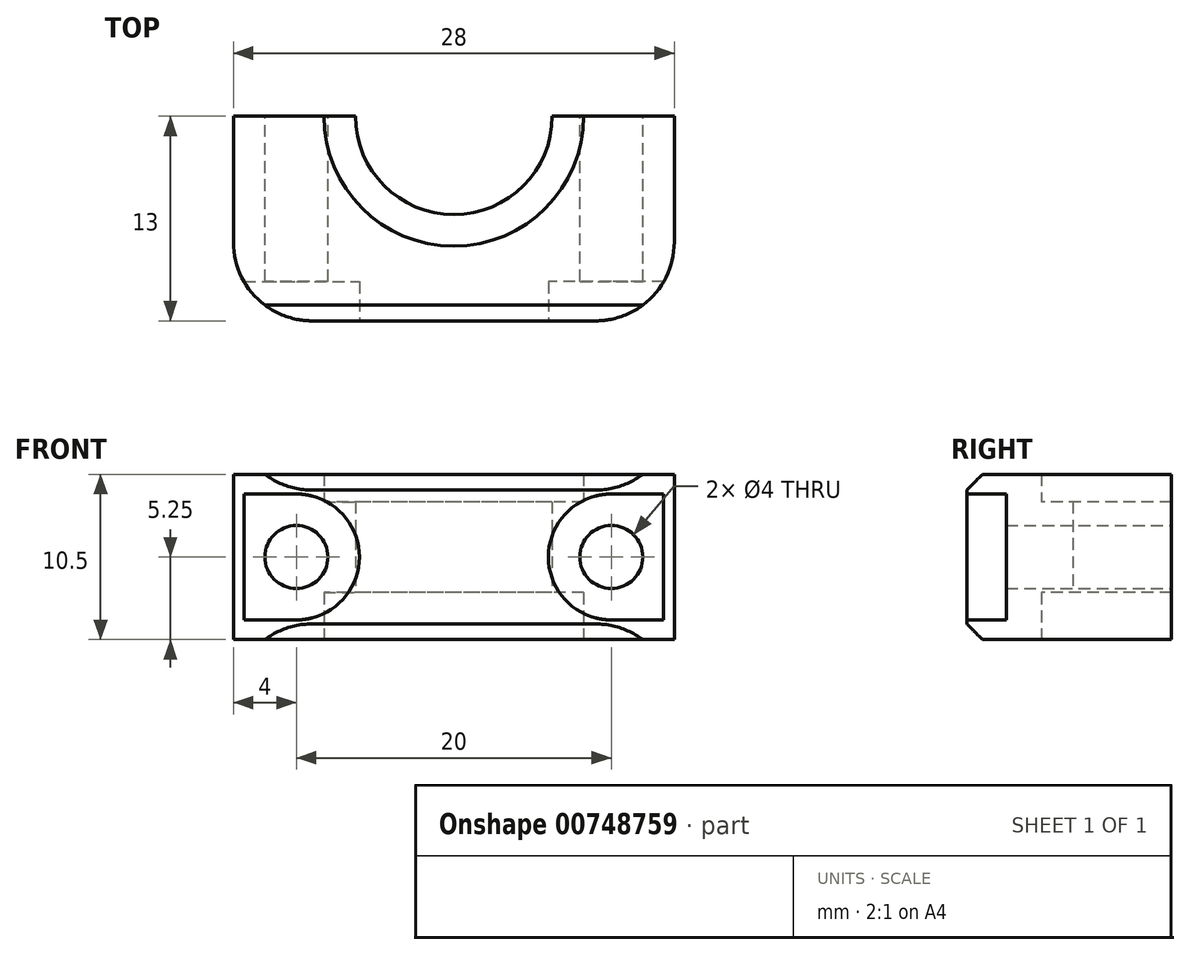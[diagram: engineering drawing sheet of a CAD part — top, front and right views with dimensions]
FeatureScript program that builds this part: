
annotation { "Feature Type Name" : "Feature", "Feature Type Description" : "" }
export const myFeature = defineFeature(function(context is Context, id is Id, definition is map)
    precondition{}
    {
        {
            var Q0;
            Q0=qCreatedBy(makeId("Front.planeOp"),FACE);
            var sketch = newSketch(context, id + "F0", { "sketchPlane" : qUnion([Q0])});
            skLineSegment(sketch, "E0", {"start": v(0, 5.25) * mm, "end": v(0, -5.25) * mm});
            skLineSegment(sketch, "E1", {"start": v(0, 5.25) * mm, "end": v(-14, 5.25) * mm});
            skLineSegment(sketch, "E2", {"start": v(-14, 5.25) * mm, "end": v(-14, -5.25) * mm});
            skLineSegment(sketch, "E3", {"start": v(0, -5.25) * mm, "end": v(-14, -5.25) * mm});
            skLineSegment(sketch, "E4", {"start": v(0, 3.5) * mm, "end": v(-8.25, 3.5) * mm});
            skLineSegment(sketch, "E5", {"start": v(-8.25, 3.5) * mm, "end": v(-8.25, 5.25) * mm});
            skLineSegment(sketch, "E6", {"start": v(0, -2.25) * mm, "end": v(-8.25, -2.25) * mm});
            skLineSegment(sketch, "E7", {"start": v(-8.25, -2.25) * mm, "end": v(-8.25, -5.25) * mm});
            skLineSegment(sketch, "E8", {"start": v(-6.25, -2.25) * mm, "end": v(-6.25, 3.5) * mm});
            skCircle(sketch, "E9", {"center": v(-10, 0) * mm, "radius": 2 * mm});
            skSolve(sketch);
        }
        {
            var Q0;
            {var subQ1=sQuery(id+"F0.wireOp",EDGE,"E2");Q0=makeQuery(id+"F0.imprint","IMPRINT",FACE,{"disambiguationData":[TD([[makeQuery(id+"F0.imprint","IMPRINT",EDGE,{"derivedFrom":subQ1}),1.0]])]});}
            var Q1;
            Q1=makeQuery(id+"F0.imprint","IMPRINT",FACE,{"disambiguationData":[TD([[makeQuery(id+"F0.imprint","IMPRINT",EDGE,{"derivedFrom":sQuery(id+"F0.wireOp",EDGE,"E9")}),1.0]])]});
            var Q2;
            {var subQ0=sQuery(id+"F0.wireOp",EDGE,"E5");Q2=makeQuery(id+"F0.imprint","IMPRINT",FACE,{"disambiguationData":[TD([[makeQuery(id+"F0.imprint","IMPRINT",EDGE,{"derivedFrom":subQ0}),-1.0]])]});}
            var Q3;
            {var subQ5=sQuery(id+"F0.wireOp",EDGE,"E8");Q3=makeQuery(id+"F0.imprint","IMPRINT",FACE,{"disambiguationData":[TD([[makeQuery(id+"F0.imprint","IMPRINT",EDGE,{"derivedFrom":subQ5}),-1.0]])]});}
            var Q4;
            {var subQ6=sQuery(id+"F0.wireOp",EDGE,"E7");Q4=makeQuery(id+"F0.imprint","IMPRINT",FACE,{"disambiguationData":[TD([[makeQuery(id+"F0.imprint","IMPRINT",EDGE,{"derivedFrom":subQ6}),1.0]])]});}
            extrude(context, id + "F1", {"entities" : qUnion([Q0, Q1, Q2, Q3, Q4]), "depth" : (8 + 5) * mm, "offsetDistance" : 25 * mm});
        }
        {
            var Q0;
            {var subQ0=sQuery(id+"F0.wireOp",EDGE,"E5");Q0=makeQuery(id+"F0.imprint","IMPRINT",FACE,{"disambiguationData":[TD([[makeQuery(id+"F0.imprint","IMPRINT",EDGE,{"derivedFrom":subQ0}),-1.0]])]});}
            var Q1;
            {var subQ5=sQuery(id+"F0.wireOp",EDGE,"E8");Q1=makeQuery(id+"F0.imprint","IMPRINT",FACE,{"disambiguationData":[TD([[makeQuery(id+"F0.imprint","IMPRINT",EDGE,{"derivedFrom":subQ5}),-1.0]])]});}
            var Q2;
            {var subQ6=sQuery(id+"F0.wireOp",EDGE,"E7");Q2=makeQuery(id+"F0.imprint","IMPRINT",FACE,{"disambiguationData":[TD([[makeQuery(id+"F0.imprint","IMPRINT",EDGE,{"derivedFrom":subQ6}),1.0]])]});}
            var Q3;
            Q3=sQuery(id+"F0.wireOp",EDGE,"E0");
            revolve(context, id + "F2", {"operationType" : NewBodyOperationType.REMOVE, "surfaceOperationType" : NewSurfaceOperationType.NEW, "entities" : qUnion([Q0, Q1, Q2]), "axis" : qUnion([Q3]), "revolveType" : RevolveType.FULL, "oppositeDirection" : true});
        }
        {
            var Q0;
            Q0=makeQuery(id+"F0.imprint","IMPRINT",FACE,{"disambiguationData":[TD([[makeQuery(id+"F0.imprint","IMPRINT",EDGE,{"derivedFrom":sQuery(id+"F0.wireOp",EDGE,"E9")}),1.0]])]});
            extrude(context, id + "F3", {"entities" : qUnion([Q0]), "operationType" : NewBodyOperationType.REMOVE, "depth" : 25 * mm, "offsetDistance" : 25 * mm});
        }
        {
            var Q0;
            Q0=makeQuery(id+"F1.opExtrude","CAP_EDGE",EDGE,{"disambiguationData":[OSD([sQuery(id+"F0.wireOp",EDGE,"E2")])],"isStart":false});
            fillet(context, id + "F4", {"entities" : qUnion([Q0]), "radius" : 5 * mm, "tangentPropagation" : true, "allowEdgeOverflow" : false});
        }
        {
            var Q0;
            {var subQ0=makeQuery(id+"F1.opExtrude","CAP_FACE",FACE,{"disambiguationData":[OSD([sQuery(id+"F0.wireOp",EDGE,"E0"),sQuery(id+"F0.wireOp",EDGE,"E1"),sQuery(id+"F0.wireOp",EDGE,"E2"),sQuery(id+"F0.wireOp",EDGE,"E3")])],"isStart":false});Q0=makeQuery(id+"F8.boolean.opBoolean","MERGE",FACE,{"derivedFrom":[subQ0,makeQuery(id+"F8.opPattern","COPY",FACE,{"derivedFrom":subQ0,"instanceName":"1"})]});}
            var sketch = newSketch(context, id + "F5", { "sketchPlane" : qUnion([Q0])});
            skCircle(sketch, "E10", {"center": v(-10, 0) * mm, "radius": 4 * mm});
            skLineSegment(sketch, "E11", {"start": v(-10, 0) * mm, "end": v(-17.92, 0) * mm});
            skLineSegment(sketch, "E12", {"start": v(-17.92, 0) * mm, "end": v(-17.92, -4) * mm});
            skLineSegment(sketch, "E13", {"start": v(-17.92, 0) * mm, "end": v(-17.92, 4) * mm});
            skLineSegment(sketch, "E14", {"start": v(-17.92, 4) * mm, "end": v(-10, 4) * mm});
            skLineSegment(sketch, "E15", {"start": v(-10, 4) * mm, "end": v(-10, 0) * mm});
            skLineSegment(sketch, "E16", {"start": v(-17.92, -4) * mm, "end": v(-10, -4) * mm});
            skLineSegment(sketch, "E17", {"start": v(-10, -4) * mm, "end": v(-10, 0) * mm});
            skSolve(sketch);
        }
        {
            var Q0;
            {var subQ4=sQuery(id+"F5.wireOp",EDGE,"E12");Q0=makeQuery(id+"F5.imprint","IMPRINT",FACE,{"disambiguationData":[TD([[makeQuery(id+"F5.imprint","IMPRINT",EDGE,{"derivedFrom":subQ4}),1.0]])]});}
            var Q1;
            {var subQ4=sQuery(id+"F5.wireOp",EDGE,"E13");Q1=makeQuery(id+"F5.imprint","IMPRINT",FACE,{"disambiguationData":[TD([[makeQuery(id+"F5.imprint","IMPRINT",EDGE,{"derivedFrom":subQ4}),-1.0]])]});}
            var Q2;
            {var subQ0=sQuery(id+"F5.wireOp",EDGE,"E15");Q2=makeQuery(id+"F5.imprint","IMPRINT",FACE,{"disambiguationData":[TD([[makeQuery(id+"F5.imprint","IMPRINT",EDGE,{"derivedFrom":subQ0}),-1.0]])]});}
            var Q3;
            {var subQ1=sQuery(id+"F0.wireOp",EDGE,"E2");var subQ2=makeQuery(id+"F1.opExtrude","CAP_FACE",FACE,{"disambiguationData":[OSD([sQuery(id+"F0.wireOp",EDGE,"E0"),sQuery(id+"F0.wireOp",EDGE,"E1"),subQ1,sQuery(id+"F0.wireOp",EDGE,"E3")])],"isStart":false});var subQ9=makeQuery(id+"F3.boolean.opBoolean","INTERSECT",EDGE,{"derivedFrom":[subQ2,makeQuery(id+"F3.opExtrude","SWEPT_FACE",FACE,{"disambiguationData":[OSD([sQuery(id+"F0.wireOp",EDGE,"E9")])]})]});Q3=makeQuery(id+"F5.imprint","IMPRINT",FACE,{"disambiguationData":[TD([[makeQuery(id+"F5.imprint","IMPRINT",EDGE,{"derivedFrom":subQ9}),1.0]])]});}
            var Q4;
            {var subQ8=sQuery(id+"F5.wireOp",EDGE,"E15");Q4=makeQuery(id+"F5.imprint","IMPRINT",FACE,{"disambiguationData":[TD([[makeQuery(id+"F5.imprint","IMPRINT",EDGE,{"derivedFrom":subQ8}),1.0]])]});}
            var Q5;
            {var subQ0=sQuery(id+"F5.wireOp",EDGE,"E17");Q5=makeQuery(id+"F5.imprint","IMPRINT",FACE,{"disambiguationData":[TD([[makeQuery(id+"F5.imprint","IMPRINT",EDGE,{"derivedFrom":subQ0}),1.0]])]});}
            extrude(context, id + "F6", {"entities" : qUnion([Q0, Q1, Q2, Q3, Q4, Q5]), "operationType" : NewBodyOperationType.REMOVE, "oppositeDirection" : true, "depth" : 2.5 * mm, "offsetDistance" : 25 * mm});
        }
        {
            var Q0;
            Q0=makeQuery(id+"F1.opExtrude","CAP_EDGE",EDGE,{"disambiguationData":[OSD([sQuery(id+"F0.wireOp",EDGE,"E3")])],"isStart":false});
            var Q1;
            Q1=makeQuery(id+"F1.opExtrude","CAP_EDGE",EDGE,{"disambiguationData":[OSD([sQuery(id+"F0.wireOp",EDGE,"E1")])],"isStart":false});
            chamfer(context, id + "F7", {"entities" : qUnion([Q0, Q1]), "width" : 1 * mm});
        }
        {
            var Q0;
            Q0=makeQuery(id+"F1.opExtrude","SWEPT_BODY",BODY,{"disambiguationData":[OSD([sQuery(id+"F0.wireOp",EDGE,"E0"),sQuery(id+"F0.wireOp",EDGE,"E1"),sQuery(id+"F0.wireOp",EDGE,"E2"),sQuery(id+"F0.wireOp",EDGE,"E3")])]});
            var Q1;
            Q1=makeQuery(id+"F1.opExtrude","SWEPT_FACE",FACE,{"disambiguationData":[OSD([sQuery(id+"F0.wireOp",EDGE,"E0")])]});
            mirror(context, id + "F8", {"operationType" : NewBodyOperationType.ADD, "entities" : qUnion([Q0]), "mirrorPlane" : qUnion([Q1])});
        }
    });
